# Revit family: lr85
name_source: partatom
category: Conduit Fittings
revit_build: Autodesk Revit 2018 (Build: 20180423_1000(x64)
units: mm (PartAtom-declared; Revit-internal decimal feet)

## family parameters
Always vertical = No
Cut with Voids When Loaded = No
Part Type = Multi Port
Round Connector Dimension = Use Diameter
Shared = No
Work Plane-Based = No

## types (1)
- LR
    A = 0' - 6 1/16"
    ARTICLENO = NB
    B = 1' - 1 1/16"
    BOMINFO = LINA
    C = 0' - 4 21/32"
    CT = Rigid/IMC
    D = 3"
    Description = Commercial Fittings
    Keynote = LR85
    LINA = LR85
    LOD = High Level of Details
    MODELS = Body
    Manufacturer = COOPERCROUSEHINDS
    Model = LR85
    NB = LR85
    NBSYN = $PNHELP.$LOD.
    NN = Condulet® Series 5 Conduit Outlet Bodies
    NT = Commercial Fittings
    PN = LR85
    SHAPE = LR
    SIZE = 3"
    SUPPLIER = COOPERCROUSEHINDS
    URL = http://www.cadenas.de
    WT = 600
    Weight = 0

## geometry (parser evidence)
native form markers: Sweep x9
no freeform markers — native parametric forms only
